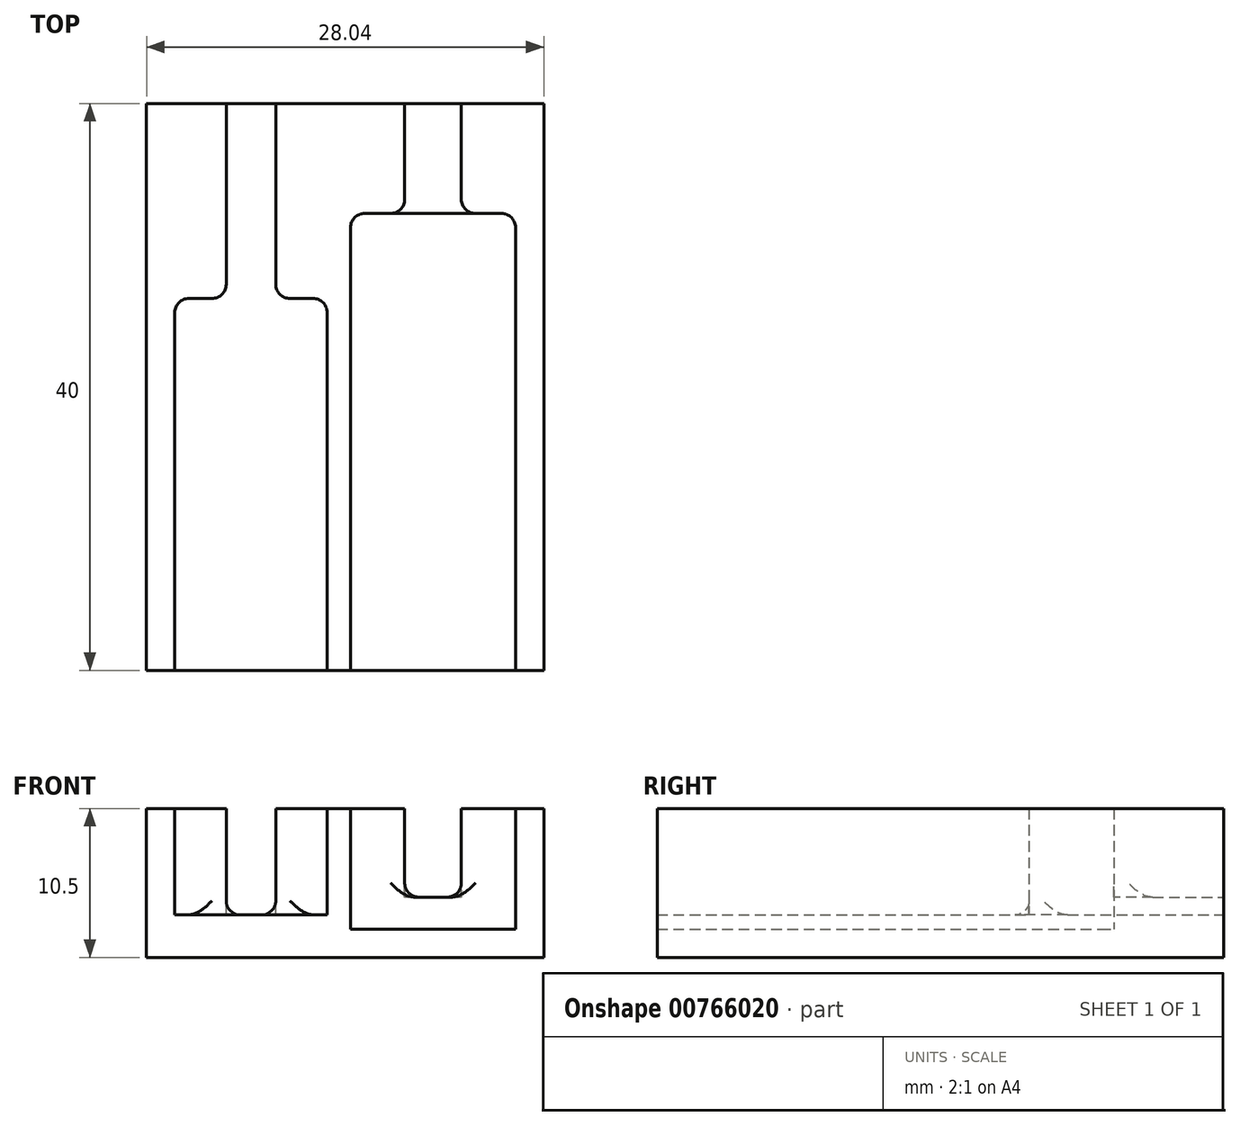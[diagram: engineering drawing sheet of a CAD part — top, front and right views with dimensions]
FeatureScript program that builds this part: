
annotation { "Feature Type Name" : "Feature", "Feature Type Description" : "" }
export const myFeature = defineFeature(function(context is Context, id is Id, definition is map)
    precondition{}
    {
        {
            var Q0;
            Q0=qCreatedBy(makeId("Top.planeOp"),FACE);
            var sketch = newSketch(context, id + "F0", { "sketchPlane" : qUnion([Q0])});
            skLineSegment(sketch, "E0.bottom", {"start": v(14.02, -20) * mm, "end": v(-14.02, -20) * mm});
            skLineSegment(sketch, "E0.top", {"start": v(14.02, 20) * mm, "end": v(-14.02, 20) * mm});
            skLineSegment(sketch, "E0.left", {"start": v(14.02, -20) * mm, "end": v(14.02, 20) * mm});
            skLineSegment(sketch, "E0.right", {"start": v(-14.02, -20) * mm, "end": v(-14.02, 20) * mm});
            skPoint(sketch, "E0.middle", {"position": v(0, 0) * mm});
            skLineSegment(sketch, "E1.bottom", {"start": v(-12.02, -20) * mm, "end": v(-1.27, -20) * mm});
            skLineSegment(sketch, "E1.top", {"start": v(-12.02, 6.25) * mm, "end": v(-1.27, 6.25) * mm});
            skLineSegment(sketch, "E1.left", {"start": v(-12.02, -20) * mm, "end": v(-12.02, 6.25) * mm});
            skLineSegment(sketch, "E1.right", {"start": v(-1.27, -20) * mm, "end": v(-1.27, 6.25) * mm});
            skLineSegment(sketch, "E2.bottom", {"start": v(0.38, -20) * mm, "end": v(12.02, -20) * mm});
            skLineSegment(sketch, "E2.top", {"start": v(0.37, 12.25) * mm, "end": v(12.03, 12.25) * mm});
            skLineSegment(sketch, "E2.left", {"start": v(0.38, -20) * mm, "end": v(0.37, 12.25) * mm});
            skLineSegment(sketch, "E2.right", {"start": v(12.02, -20) * mm, "end": v(12.02, 12.25) * mm});
            skLineSegment(sketch, "E3", {"start": v(-6.65, 6.25) * mm, "end": v(-6.65, 20) * mm, "construction": true});
            skLineSegment(sketch, "E4.bottom", {"start": v(-4.9, 6.25) * mm, "end": v(-8.4, 6.25) * mm});
            skLineSegment(sketch, "E4.top", {"start": v(-4.9, 20) * mm, "end": v(-8.4, 20) * mm});
            skLineSegment(sketch, "E4.left", {"start": v(-4.9, 6.25) * mm, "end": v(-4.9, 20) * mm});
            skLineSegment(sketch, "E4.right", {"start": v(-8.4, 6.25) * mm, "end": v(-8.4, 20) * mm});
            skPoint(sketch, "E4.middle", {"position": v(-6.65, 13.12) * mm});
            skLineSegment(sketch, "E5", {"start": v(6.2, 12.25) * mm, "end": v(6.2, 20) * mm, "construction": true});
            skLineSegment(sketch, "E6.bottom", {"start": v(8.2, 12.25) * mm, "end": v(4.2, 12.25) * mm});
            skLineSegment(sketch, "E6.top", {"start": v(8.2, 20) * mm, "end": v(4.2, 20) * mm});
            skLineSegment(sketch, "E6.left", {"start": v(8.2, 12.25) * mm, "end": v(8.2, 20) * mm});
            skLineSegment(sketch, "E6.right", {"start": v(4.2, 12.25) * mm, "end": v(4.2, 20) * mm});
            skPoint(sketch, "E6.middle", {"position": v(6.2, 16.12) * mm});
            skSolve(sketch);
        }
        {
            var Q0;
            {var subQ3=sQuery(id+"F0.wireOp",EDGE,"E1.left");Q0=makeQuery(id+"F0.imprint","IMPRINT",FACE,{"disambiguationData":[TD([[makeQuery(id+"F0.imprint","IMPRINT",EDGE,{"derivedFrom":subQ3}),-1.0]])]});}
            var Q1;
            {var subQ3=sQuery(id+"F0.wireOp",EDGE,"E0.right");Q1=makeQuery(id+"F0.imprint","IMPRINT",FACE,{"disambiguationData":[TD([[makeQuery(id+"F0.imprint","IMPRINT",EDGE,{"derivedFrom":subQ3}),-1.0]])]});}
            var Q2;
            {var subQ0=sQuery(id+"F0.wireOp",EDGE,"E1.right");Q2=makeQuery(id+"F0.imprint","IMPRINT",FACE,{"disambiguationData":[TD([[makeQuery(id+"F0.imprint","IMPRINT",EDGE,{"derivedFrom":subQ0}),-1.0]])]});}
            var Q3;
            {var subQ2=sQuery(id+"F0.wireOp",EDGE,"E4.left");Q3=makeQuery(id+"F0.imprint","IMPRINT",FACE,{"disambiguationData":[TD([[makeQuery(id+"F0.imprint","IMPRINT",EDGE,{"derivedFrom":subQ2}),1.0]])]});}
            var Q4;
            {var subQ2=sQuery(id+"F0.wireOp",EDGE,"E6.left");Q4=makeQuery(id+"F0.imprint","IMPRINT",FACE,{"disambiguationData":[TD([[makeQuery(id+"F0.imprint","IMPRINT",EDGE,{"derivedFrom":subQ2}),1.0]])]});}
            var Q5;
            {var subQ4=sQuery(id+"F0.wireOp",EDGE,"E2.left");Q5=makeQuery(id+"F0.imprint","IMPRINT",FACE,{"disambiguationData":[TD([[makeQuery(id+"F0.imprint","IMPRINT",EDGE,{"derivedFrom":subQ4}),-1.0]])]});}
            var Q6;
            {var subQ3=sQuery(id+"F0.wireOp",EDGE,"E0.left");Q6=makeQuery(id+"F0.imprint","IMPRINT",FACE,{"disambiguationData":[TD([[makeQuery(id+"F0.imprint","IMPRINT",EDGE,{"derivedFrom":subQ3}),1.0]])]});}
            extrude(context, id + "F1", {"entities" : qUnion([Q0, Q1, Q2, Q3, Q4, Q5, Q6]), "oppositeDirection" : true, "depth" : 2 * mm, "offsetDistance" : 25 * mm});
        }
        {
            var Q0;
            {var subQ3=sQuery(id+"F0.wireOp",EDGE,"E0.right");Q0=makeQuery(id+"F0.imprint","IMPRINT",FACE,{"disambiguationData":[TD([[makeQuery(id+"F0.imprint","IMPRINT",EDGE,{"derivedFrom":subQ3}),-1.0]])]});}
            var Q1;
            {var subQ0=sQuery(id+"F0.wireOp",EDGE,"E1.right");Q1=makeQuery(id+"F0.imprint","IMPRINT",FACE,{"disambiguationData":[TD([[makeQuery(id+"F0.imprint","IMPRINT",EDGE,{"derivedFrom":subQ0}),-1.0]])]});}
            var Q2;
            {var subQ3=sQuery(id+"F0.wireOp",EDGE,"E0.left");Q2=makeQuery(id+"F0.imprint","IMPRINT",FACE,{"disambiguationData":[TD([[makeQuery(id+"F0.imprint","IMPRINT",EDGE,{"derivedFrom":subQ3}),1.0]])]});}
            extrude(context, id + "F2", {"entities" : qUnion([Q0, Q1, Q2]), "operationType" : NewBodyOperationType.ADD, "depth" : 8.5 * mm, "offsetDistance" : 25 * mm});
        }
        {
            var Q0;
            {var subQ3=sQuery(id+"F0.wireOp",EDGE,"E1.left");Q0=makeQuery(id+"F0.imprint","IMPRINT",FACE,{"disambiguationData":[TD([[makeQuery(id+"F0.imprint","IMPRINT",EDGE,{"derivedFrom":subQ3}),-1.0]])]});}
            var Q1;
            {var subQ2=sQuery(id+"F0.wireOp",EDGE,"E4.left");Q1=makeQuery(id+"F0.imprint","IMPRINT",FACE,{"disambiguationData":[TD([[makeQuery(id+"F0.imprint","IMPRINT",EDGE,{"derivedFrom":subQ2}),1.0]])]});}
            extrude(context, id + "F3", {"entities" : qUnion([Q0, Q1]), "operationType" : NewBodyOperationType.ADD, "depth" : 1 * mm, "offsetDistance" : 25 * mm});
        }
        {
            var Q0;
            {var subQ2=sQuery(id+"F0.wireOp",EDGE,"E6.left");Q0=makeQuery(id+"F0.imprint","IMPRINT",FACE,{"disambiguationData":[TD([[makeQuery(id+"F0.imprint","IMPRINT",EDGE,{"derivedFrom":subQ2}),1.0]])]});}
            extrude(context, id + "F4", {"entities" : qUnion([Q0]), "operationType" : NewBodyOperationType.ADD, "depth" : 2.25 * mm, "offsetDistance" : 25 * mm});
        }
        {
            var Q0;
            Q0=makeQuery(id+"F2.opExtrude","SWEPT_EDGE",EDGE,{"disambiguationData":[OSD([sQuery(id+"F0.wireOp",EDGE,"E1.top"),sQuery(id+"F0.wireOp",EDGE,"E1.left")])]});
            var Q1;
            Q1=makeQuery(id+"F2.opExtrude","SWEPT_EDGE",EDGE,{"disambiguationData":[OSD([sQuery(id+"F0.wireOp",EDGE,"E1.top"),sQuery(id+"F0.wireOp",EDGE,"E4.right")])]});
            var Q2;
            Q2=makeQuery(id+"F2.opExtrude","SWEPT_EDGE",EDGE,{"disambiguationData":[OSD([sQuery(id+"F0.wireOp",EDGE,"E1.top"),sQuery(id+"F0.wireOp",EDGE,"E4.left")])]});
            var Q3;
            Q3=makeQuery(id+"F2.opExtrude","SWEPT_EDGE",EDGE,{"disambiguationData":[OSD([sQuery(id+"F0.wireOp",EDGE,"E1.top"),sQuery(id+"F0.wireOp",EDGE,"E1.right")])]});
            var Q4;
            Q4=makeQuery(id+"F2.opExtrude","SWEPT_EDGE",EDGE,{"disambiguationData":[OSD([sQuery(id+"F0.wireOp",EDGE,"E2.top"),sQuery(id+"F0.wireOp",EDGE,"E6.right")])]});
            var Q5;
            Q5=makeQuery(id+"F2.opExtrude","SWEPT_EDGE",EDGE,{"disambiguationData":[OSD([sQuery(id+"F0.wireOp",EDGE,"E2.top"),sQuery(id+"F0.wireOp",EDGE,"E6.left")])]});
            var Q6;
            Q6=makeQuery(id+"F2.opExtrude","SWEPT_EDGE",EDGE,{"disambiguationData":[OSD([sQuery(id+"F0.wireOp",EDGE,"E2.top"),sQuery(id+"F0.wireOp",EDGE,"E2.left")])]});
            var Q7;
            Q7=makeQuery(id+"F2.opExtrude","SWEPT_EDGE",EDGE,{"disambiguationData":[OSD([sQuery(id+"F0.wireOp",EDGE,"E2.top"),sQuery(id+"F0.wireOp",EDGE,"E2.right")])]});
            fillet(context, id + "F5", {"entities" : qUnion([Q0, Q1, Q2, Q3, Q4, Q5, Q6, Q7]), "radius" : 1 * mm, "tangentPropagation" : true, "allowEdgeOverflow" : false});
        }
        {
            var Q0;
            Q0=makeQuery(id+"F3.opExtrude","CAP_EDGE",EDGE,{"disambiguationData":[OSD([sQuery(id+"F0.wireOp",EDGE,"E4.right")])],"isStart":false});
            var Q1;
            {var subQ0=sQuery(id+"F0.wireOp",EDGE,"E4.right");var subQ1=sQuery(id+"F0.wireOp",EDGE,"E1.top");Q1=makeQuery(id+"F5.opFillet","BLEND_EDGE",EDGE,{"blendedFrom":[makeQuery(id+"F2.opExtrude","SWEPT_EDGE",EDGE,{"disambiguationData":[OSD([subQ1,subQ0])]}),makeQuery(id+"F3.opExtrude","CAP_FACE",FACE,{"disambiguationData":[OSD([sQuery(id+"F0.wireOp",EDGE,"E0.bottom"),sQuery(id+"F0.wireOp",EDGE,"E0.top"),subQ1,sQuery(id+"F0.wireOp",EDGE,"E1.left"),sQuery(id+"F0.wireOp",EDGE,"E1.right"),sQuery(id+"F0.wireOp",EDGE,"E4.left"),subQ0])],"isStart":false})],"blendedInto":[makeQuery(id+"F3.opExtrude","CAP_FACE",FACE,{"disambiguationData":[OSD([sQuery(id+"F0.wireOp",EDGE,"E0.bottom"),sQuery(id+"F0.wireOp",EDGE,"E0.top"),subQ1,sQuery(id+"F0.wireOp",EDGE,"E1.left"),sQuery(id+"F0.wireOp",EDGE,"E1.right"),sQuery(id+"F0.wireOp",EDGE,"E4.left"),subQ0])],"isStart":false})]});}
            var Q2;
            Q2=makeQuery(id+"F3.opExtrude","CAP_EDGE",EDGE,{"disambiguationData":[OSD([sQuery(id+"F0.wireOp",EDGE,"E4.left")])],"isStart":false});
            var Q3;
            {var subQ0=sQuery(id+"F0.wireOp",EDGE,"E4.left");var subQ1=sQuery(id+"F0.wireOp",EDGE,"E1.top");Q3=makeQuery(id+"F5.opFillet","BLEND_EDGE",EDGE,{"blendedFrom":[makeQuery(id+"F2.opExtrude","SWEPT_EDGE",EDGE,{"disambiguationData":[OSD([subQ1,subQ0])]}),makeQuery(id+"F3.opExtrude","CAP_FACE",FACE,{"disambiguationData":[OSD([sQuery(id+"F0.wireOp",EDGE,"E0.bottom"),sQuery(id+"F0.wireOp",EDGE,"E0.top"),subQ1,sQuery(id+"F0.wireOp",EDGE,"E1.left"),sQuery(id+"F0.wireOp",EDGE,"E1.right"),subQ0,sQuery(id+"F0.wireOp",EDGE,"E4.right")])],"isStart":false})],"blendedInto":[makeQuery(id+"F3.opExtrude","CAP_FACE",FACE,{"disambiguationData":[OSD([sQuery(id+"F0.wireOp",EDGE,"E0.bottom"),sQuery(id+"F0.wireOp",EDGE,"E0.top"),subQ1,sQuery(id+"F0.wireOp",EDGE,"E1.left"),sQuery(id+"F0.wireOp",EDGE,"E1.right"),subQ0,sQuery(id+"F0.wireOp",EDGE,"E4.right")])],"isStart":false})]});}
            var Q4;
            {var subQ0=sQuery(id+"F0.wireOp",EDGE,"E6.right");var subQ1=sQuery(id+"F0.wireOp",EDGE,"E2.top");Q4=makeQuery(id+"F5.opFillet","BLEND_EDGE",EDGE,{"blendedFrom":[makeQuery(id+"F2.opExtrude","SWEPT_EDGE",EDGE,{"disambiguationData":[OSD([subQ1,subQ0])]}),makeQuery(id+"F4.opExtrude","CAP_FACE",FACE,{"disambiguationData":[OSD([sQuery(id+"F0.wireOp",EDGE,"E0.top"),subQ1,sQuery(id+"F0.wireOp",EDGE,"E6.left"),subQ0])],"isStart":false})],"blendedInto":[makeQuery(id+"F4.opExtrude","CAP_FACE",FACE,{"disambiguationData":[OSD([sQuery(id+"F0.wireOp",EDGE,"E0.top"),subQ1,sQuery(id+"F0.wireOp",EDGE,"E6.left"),subQ0])],"isStart":false})]});}
            var Q5;
            Q5=makeQuery(id+"F4.opExtrude","CAP_EDGE",EDGE,{"disambiguationData":[OSD([sQuery(id+"F0.wireOp",EDGE,"E6.right")])],"isStart":false});
            var Q6;
            {var subQ0=sQuery(id+"F0.wireOp",EDGE,"E6.left");var subQ1=sQuery(id+"F0.wireOp",EDGE,"E2.top");Q6=makeQuery(id+"F5.opFillet","BLEND_EDGE",EDGE,{"blendedFrom":[makeQuery(id+"F2.opExtrude","SWEPT_EDGE",EDGE,{"disambiguationData":[OSD([subQ1,subQ0])]}),makeQuery(id+"F4.opExtrude","CAP_FACE",FACE,{"disambiguationData":[OSD([sQuery(id+"F0.wireOp",EDGE,"E0.top"),subQ1,subQ0,sQuery(id+"F0.wireOp",EDGE,"E6.right")])],"isStart":false})],"blendedInto":[makeQuery(id+"F4.opExtrude","CAP_FACE",FACE,{"disambiguationData":[OSD([sQuery(id+"F0.wireOp",EDGE,"E0.top"),subQ1,subQ0,sQuery(id+"F0.wireOp",EDGE,"E6.right")])],"isStart":false})]});}
            var Q7;
            Q7=makeQuery(id+"F4.opExtrude","CAP_EDGE",EDGE,{"disambiguationData":[OSD([sQuery(id+"F0.wireOp",EDGE,"E6.left")])],"isStart":false});
            fillet(context, id + "F6", {"entities" : qUnion([Q0, Q1, Q2, Q3, Q4, Q5, Q6, Q7]), "radius" : 1 * mm, "allowEdgeOverflow" : false});
        }
    });
